# Revit family: NBS_DudleyIndustries_PprTwlDpnsrs_PlasmaRange_LargePaperTowelDispenser
name_source: partatom
category: Specialty Equipment
revit_build: Autodesk Revit 2016 (Build: 20150220_1215(x64)
units: mm (PartAtom-declared; Revit-internal decimal feet)

## family parameters
Cut with Voids When Loaded = No
Host = Face
OmniClass Number = 23.40.20.21.17
OmniClass Title = Paper Towel Dispensers, Disposal Units
Part Type = Normal
Room Calculation Point = No
Round Connector Dimension = Use Diameter
Shared = No

## types (1)
- PlasmaRangeLargePaperTowelDispenser
    AssetType = Fixed
    BIMObjectName = NBS_DudleyIndustries_PaperTowelDispensers_PlasmaRange_LargePaperTowelDispenser
    Category = Pr_40_70_22_62:Paper towel dispensers
    Color = Stainless steel
    Default Elevation = 1200 mm
    Description = Paper towel dispenser
    DispenserCabinetMaterial = NBS_Concept
    DispenserLockMaterial = NBS_Concept
    DurationUnit = year
    ExpectedLife = 5
    Features = Robust stainless steel construction which protects paper from spoiling, excellent for demanding locations, locking mechanism, designed for either C fold or multi-fold interleaved paper hand towels
    Finish = Brushed (78805SS), Polished (78805PS), White Powder Coated (78805WH)
    Form = Wall mounted
    Grade = 304
    IfcExportAs = IfcFurnitureType
    IfcExportType = NOTDEFINED
    MainColor = Stainless steel
    ManufacturerName = Dudley Industries
    ManufacturerURL = www.dudleyindustries.com/
    Material = Stainless steel
    MaterialsBody = 304 Stainless steel
    MaterialsFinishColour = Brushed (78805SS), Polished (78805PS), White Powder Coated (78805WH)
    ModelNumber = 78805
    ModelReference = Plasma Range: Large Paper Towel Dispenser
    NBSCertification = www.nationalbimlibrary.com/cert/mk353luu
    NBSDescription = Paper towel dispensers
    NBSReference = 45-35-72/344
    Name = PaperTowelDispensers_PlasmaRange_LargePaperTowelDispenser_DudleyIndustries
    NominalDepth = 124 mm  [stored 0.406824 ft]
    NominalHeight = 378 mm  [stored 1.24016 ft]
    NominalLength = 260 mm  [stored 0.853018 ft]
    NominalWidth = 260 mm  [stored 0.853018 ft]
    Operation = Manual
    ProductInformation = www.dudleyindustries.com/wp-content/uploads/2016/11/CMulti-fold-Large-Paper-Towel-Dispenser-1.pdf
    Size = 260 x 378 x 124 mm
    Style = Paper Towel Dispenser
    TowelsTowelType = C fold or multi-fold interleaved
    TowelsWidth = 250 mm max
    Uniclass2015Code = Pr_40_70_22_62
    Uniclass2015Title = Paper towel dispensers
    Uniclass2015Version = Products v1.7
    Version = 2
    WarrantyDescription = 1 year warranty
    WarrantyDurationParts = 1
    WarrantyDurationUnit = year

note: [stored X ft] marks values corroborated as IEEE doubles in the binary element streams (Revit-internal decimal feet)

## geometry (parser evidence)
native form markers: Sweep x2
no freeform markers — native parametric forms only
